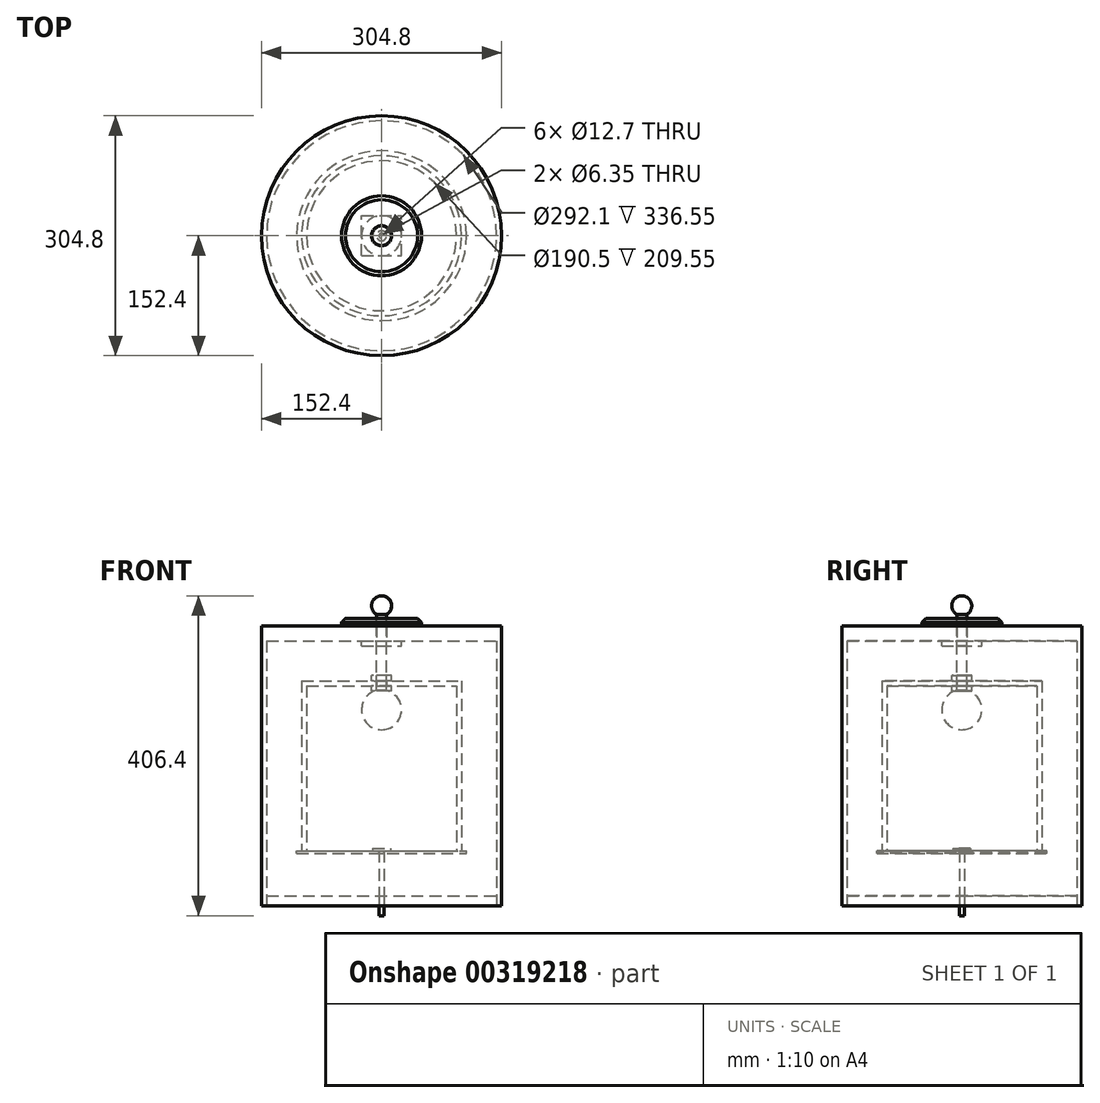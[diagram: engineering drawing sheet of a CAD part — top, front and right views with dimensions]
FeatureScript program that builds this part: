
annotation { "Feature Type Name" : "Feature", "Feature Type Description" : "" }
export const myFeature = defineFeature(function(context is Context, id is Id, definition is map)
    precondition{}
    {
        {
            var Q0;
            Q0=qCreatedBy(makeId("Front.planeOp"),FACE);
            var sketch = newSketch(context, id + "F0", { "sketchPlane" : qUnion([Q0])});
            skLineSegment(sketch, "E0", {"start": v(6.35, 0) * mm, "end": v(152.4, 0) * mm});
            skLineSegment(sketch, "E1", {"start": v(152.4, 0) * mm, "end": v(152.4, -355.6) * mm});
            skLineSegment(sketch, "E2", {"start": v(152.4, -355.6) * mm, "end": v(146.05, -355.6) * mm});
            skLineSegment(sketch, "E3", {"start": v(0, -400.05) * mm, "end": v(0, -355.6) * mm});
            skLineSegment(sketch, "E4", {"start": v(146.05, -349.25) * mm, "end": v(146.05, -19.05) * mm});
            skLineSegment(sketch, "E5", {"start": v(146.05, -19.05) * mm, "end": v(6.35, -19.05) * mm});
            skLineSegment(sketch, "E6", {"start": v(6.35, 0) * mm, "end": v(6.35, -19.05) * mm});
            skPoint(sketch, "E7.orphan", {"position": v(0, -19.05) * mm});
            skLineSegment(sketch, "E8", {"start": v(146.05, -349.25) * mm, "end": v(146.05, -355.6) * mm});
            skSolve(sketch);
        }
        {
            var Q0;
            Q0=makeQuery(id+"F0.imprint","IMPRINT",FACE,{"disambiguationData":[TD([[makeQuery(id+"F0.imprint","IMPRINT",EDGE,{"derivedFrom":sQuery(id+"F0.wireOp",EDGE,"E0")}),-1.0]])]});
            var Q1;
            Q1=sQuery(id+"F0.wireOp",EDGE,"E3");
            revolve(context, id + "F1", {"entities" : qUnion([Q0]), "axis" : qUnion([Q1]), "revolveType" : RevolveType.FULL});
        }
        {
            var Q0;
            Q0=qCreatedBy(makeId("Front.planeOp"),FACE);
            var sketch = newSketch(context, id + "F2", { "sketchPlane" : qUnion([Q0])});
            skLineSegment(sketch, "E9", {"start": v(0, 0) * mm, "end": v(50.8, 0) * mm});
            skLineSegment(sketch, "E10", {"start": v(50.8, 0) * mm, "end": v(50.8, 9.53) * mm});
            skLineSegment(sketch, "E11", {"start": v(50.8, 9.53) * mm, "end": v(6.35, 9.52) * mm});
            skLineSegment(sketch, "E12", {"start": v(0, 12.7) * mm, "end": v(0, 0) * mm});
            skLineSegment(sketch, "E13", {"start": v(6.35, 9.52) * mm, "end": v(6.35, 0) * mm});
            skSolve(sketch);
        }
        {
            var Q0;
            Q0=makeQuery(id+"F2.imprint","IMPRINT",FACE,{"disambiguationData":[TD([[makeQuery(id+"F2.imprint","IMPRINT",EDGE,{"derivedFrom":sQuery(id+"F2.wireOp",EDGE,"E9")}),1.0]])]});
            var Q1;
            Q1=sQuery(id+"F2.wireOp",EDGE,"E12");
            revolve(context, id + "F3", {"entities" : qUnion([Q0]), "axis" : qUnion([Q1]), "revolveType" : RevolveType.FULL});
        }
        {
            var Q0;
            Q0=qCreatedBy(makeId("Front.planeOp"),FACE);
            var sketch = newSketch(context, id + "F4", { "sketchPlane" : qUnion([Q0])});
            skLineSegment(sketch, "E14", {"start": v(0, 0) * mm, "end": v(0, -81.28) * mm});
            skLineSegment(sketch, "E15", {"start": v(6.35, -82.09) * mm, "end": v(6.35, 0) * mm});
            skLineSegment(sketch, "E16", {"start": v(6.35, 0) * mm, "end": v(0, 0) * mm});
            skLineSegment(sketch, "E17", {"start": v(6.35, 0) * mm, "end": v(6.35, 14.4) * mm});
            skArc(sketch, "E18", {"start": v(6.35, 14.4) * mm, "mid": v(12.27, 28.69) * mm, "end": v(0, 38.1) * mm});
            skLineSegment(sketch, "E19", {"start": v(0, 0) * mm, "end": v(0, 38.1) * mm});
            skArc(sketch, "E20", {"start": v(0, -132.08) * mm, "mid": v(25.2, -109.88) * mm, "end": v(6.35, -82.09) * mm});
            skPoint(sketch, "E21.orphan", {"position": v(0, -82.55) * mm});
            skLineSegment(sketch, "E22", {"start": v(0, -81.28) * mm, "end": v(0, -132.08) * mm});
            skSolve(sketch);
        }
        {
            var Q0;
            Q0 = qSketchRegion(id + "F4", true);
            var Q1;
            Q1=sQuery(id+"F4.wireOp",EDGE,"E14");
            revolve(context, id + "F5", {"entities" : qUnion([Q0]), "axis" : qUnion([Q1]), "revolveType" : RevolveType.FULL});
        }
        {
            var Q0;
            Q0=qCreatedBy(makeId("Front.planeOp"),FACE);
            var sketch = newSketch(context, id + "F6", { "sketchPlane" : qUnion([Q0])});
            skLineSegment(sketch, "E23", {"start": v(6.35, -69.85) * mm, "end": v(101.6, -69.85) * mm});
            skLineSegment(sketch, "E24", {"start": v(101.6, -69.85) * mm, "end": v(101.6, -285.75) * mm});
            skLineSegment(sketch, "E25", {"start": v(101.6, -285.75) * mm, "end": v(95.25, -285.75) * mm});
            skLineSegment(sketch, "E26", {"start": v(0, -335.92) * mm, "end": v(0, -285.75) * mm});
            skLineSegment(sketch, "E27", {"start": v(95.25, -330.2) * mm, "end": v(95.25, -76.2) * mm});
            skLineSegment(sketch, "E28", {"start": v(95.25, -76.2) * mm, "end": v(6.35, -76.2) * mm});
            skLineSegment(sketch, "E29", {"start": v(0, -76.2) * mm, "end": v(0, -69.85) * mm});
            skLineSegment(sketch, "E30", {"start": v(95.25, -285.75) * mm, "end": v(95.25, -330.2) * mm});
            skLineSegment(sketch, "E31", {"start": v(6.35, -69.85) * mm, "end": v(6.35, -76.2) * mm});
            skSolve(sketch);
        }
        {
            var Q0;
            Q0 = qSketchRegion(id + "F6", true);
            var Q1;
            Q1=sQuery(id+"F6.wireOp",EDGE,"E29");
            revolve(context, id + "F7", {"entities" : qUnion([Q0]), "axis" : qUnion([Q1]), "revolveType" : RevolveType.FULL});
        }
        {
            var Q0;
            Q0=qCreatedBy(makeId("Front.planeOp"),FACE);
            var sketch = newSketch(context, id + "F8", { "sketchPlane" : qUnion([Q0])});
            skLineSegment(sketch, "E32.bottom", {"start": v(6.35, -69.85) * mm, "end": v(12.7, -69.85) * mm});
            skLineSegment(sketch, "E32.top", {"start": v(6.35, -63.09) * mm, "end": v(12.7, -63.09) * mm});
            skLineSegment(sketch, "E32.left", {"start": v(6.35, -69.85) * mm, "end": v(6.35, -63.09) * mm});
            skLineSegment(sketch, "E32.right", {"start": v(12.7, -69.85) * mm, "end": v(12.7, -63.09) * mm});
            skLineSegment(sketch, "E33.bottom", {"start": v(6.35, -76.2) * mm, "end": v(12.7, -76.2) * mm});
            skLineSegment(sketch, "E33.top", {"start": v(6.35, -82.96) * mm, "end": v(12.7, -82.96) * mm});
            skLineSegment(sketch, "E33.left", {"start": v(6.35, -76.2) * mm, "end": v(6.35, -82.96) * mm});
            skLineSegment(sketch, "E33.right", {"start": v(12.7, -76.2) * mm, "end": v(12.7, -82.96) * mm});
            skLineSegment(sketch, "E34", {"start": v(0, -57.88) * mm, "end": v(0, -89.68) * mm, "construction": true});
            skSolve(sketch);
        }
        {
            var Q0;
            Q0=makeQuery(id+"F8.imprint","IMPRINT",FACE,{"disambiguationData":[TD([[makeQuery(id+"F8.imprint","IMPRINT",EDGE,{"derivedFrom":sQuery(id+"F8.wireOp",EDGE,"E32.bottom")}),1.0]])]});
            var Q1;
            Q1=makeQuery(id+"F8.imprint","IMPRINT",FACE,{"disambiguationData":[TD([[makeQuery(id+"F8.imprint","IMPRINT",EDGE,{"derivedFrom":sQuery(id+"F8.wireOp",EDGE,"E33.bottom")}),-1.0]])]});
            var Q2;
            Q2=sQuery(id+"F8.wireOp",EDGE,"E34");
            revolve(context, id + "F9", {"entities" : qUnion([Q0, Q1]), "axis" : qUnion([Q2]), "revolveType" : RevolveType.FULL});
        }
        {
            var Q0;
            Q0=makeQuery(id+"F7.opRevolve","SWEPT_FACE",FACE,{"disambiguationData":[OSD([sQuery(id+"F6.wireOp",EDGE,"E25")])]});
            var sketch = newSketch(context, id + "F10", { "sketchPlane" : qUnion([Q0])});
            skCircle(sketch, "E35", {"center": v(0, 0) * mm, "radius": 107.95 * mm});
            skCircle(sketch, "E36", {"center": v(0, 0) * mm, "radius": 3.18 * mm});
            skSolve(sketch);
        }
        {
            var Q0;
            Q0=makeQuery(id+"F10.imprint","IMPRINT",FACE,{"disambiguationData":[TD([[makeQuery(id+"F10.imprint","IMPRINT",EDGE,{"derivedFrom":sQuery(id+"F10.wireOp",EDGE,"E35")}),1.0]])]});
            var Q1;
            Q1=makeQuery(id+"F10.imprint","IMPRINT",FACE,{"disambiguationData":[TD([[makeQuery(id+"F10.imprint","IMPRINT",EDGE,{"derivedFrom":makeQuery(id+"F7.opRevolve","SWEPT_EDGE",EDGE,{"disambiguationData":[OSD([sQuery(id+"F6.wireOp",EDGE,"E25"),sQuery(id+"F6.wireOp",EDGE,"E27")])]})}),1.0]])]});
            var Q2;
            {var subQ0=sQuery(id+"F6.wireOp",EDGE,"E25");Q2=makeQuery(id+"F10.imprint","IMPRINT",FACE,{"disambiguationData":[TD([[makeQuery(id+"F10.imprint","IMPRINT",EDGE,{"derivedFrom":makeQuery(id+"F7.opRevolve","SWEPT_EDGE",EDGE,{"disambiguationData":[OSD([sQuery(id+"F6.wireOp",EDGE,"E24"),subQ0])]})}),1.0]])]});}
            extrude(context, id + "F11", {"entities" : qUnion([Q0, Q1, Q2]), "depth" : 3.17 * mm});
        }
        {
            var Q0;
            Q0=makeQuery(id+"F3.opRevolve","SWEPT_EDGE",EDGE,{"disambiguationData":[OSD([sQuery(id+"F2.wireOp",EDGE,"E10"),sQuery(id+"F2.wireOp",EDGE,"E11")])]});
            chamfer(context, id + "F12", {"entities" : qUnion([Q0]), "width" : 5.08 * mm, "tangentPropagation" : true});
        }
        {
            var Q0;
            Q0=qCreatedBy(makeId("Front.planeOp"),FACE);
            var sketch = newSketch(context, id + "F13", { "sketchPlane" : qUnion([Q0])});
            skLineSegment(sketch, "E37", {"start": v(0, -282.58) * mm, "end": v(11.22, -282.58) * mm});
            skLineSegment(sketch, "E38", {"start": v(11.22, -282.58) * mm, "end": v(11.22, -285.75) * mm});
            skLineSegment(sketch, "E39", {"start": v(11.22, -285.75) * mm, "end": v(3.17, -285.75) * mm});
            skLineSegment(sketch, "E40", {"start": v(3.17, -285.75) * mm, "end": v(3.18, -368.3) * mm});
            skLineSegment(sketch, "E41", {"start": v(3.18, -368.3) * mm, "end": v(0, -368.3) * mm});
            skLineSegment(sketch, "E42", {"start": v(0, -368.3) * mm, "end": v(0, -282.58) * mm});
            skSolve(sketch);
        }
        {
            var Q0;
            Q0=makeQuery(id+"F13.imprint","IMPRINT",FACE,{"disambiguationData":[TD([[makeQuery(id+"F13.imprint","IMPRINT",EDGE,{"derivedFrom":sQuery(id+"F13.wireOp",EDGE,"E37")}),-1.0]])]});
            var Q1;
            Q1=sQuery(id+"F13.wireOp",EDGE,"E42");
            revolve(context, id + "F14", {"entities" : qUnion([Q0]), "axis" : qUnion([Q1]), "revolveType" : RevolveType.FULL});
        }
        {
            var Q0;
            Q0=makeQuery(id+"F1.opRevolve","SWEPT_FACE",FACE,{"disambiguationData":[OSD([sQuery(id+"F0.wireOp",EDGE,"E5")])]});
            var sketch = newSketch(context, id + "F15", { "sketchPlane" : qUnion([Q0])});
            skLineSegment(sketch, "E43.bottom", {"start": v(-25.4, 25.4) * mm, "end": v(25.4, 25.4) * mm});
            skLineSegment(sketch, "E43.top", {"start": v(-25.4, -25.4) * mm, "end": v(25.4, -25.4) * mm});
            skLineSegment(sketch, "E43.left", {"start": v(-25.4, 25.4) * mm, "end": v(-25.4, -25.4) * mm});
            skLineSegment(sketch, "E43.right", {"start": v(25.4, 25.4) * mm, "end": v(25.4, -25.4) * mm});
            skPoint(sketch, "E43.middle", {"position": v(0, 0) * mm});
            skSolve(sketch);
        }
        {
            var Q0;
            Q0=makeQuery(id+"F15.imprint","IMPRINT",FACE,{"disambiguationData":[TD([[makeQuery(id+"F15.imprint","IMPRINT",EDGE,{"derivedFrom":sQuery(id+"F15.wireOp",EDGE,"E43.bottom")}),-1.0]])]});
            extrude(context, id + "F16", {"entities" : qUnion([Q0]), "depth" : 6.35 * mm});
        }
        {
            var Q0;
            Q0=makeQuery(id+"F1.opRevolve","SWEPT_FACE",FACE,{"disambiguationData":[OSD([sQuery(id+"F0.wireOp",EDGE,"E2")])]});
            var sketch = newSketch(context, id + "F17", { "sketchPlane" : qUnion([Q0])});
            skCircle(sketch, "E44", {"center": v(0, 0) * mm, "radius": 146.05 * mm});
            skCircle(sketch, "E45", {"center": v(0, 0) * mm, "radius": 3.18 * mm});
            skSolve(sketch);
        }
        {
            var Q0;
            Q0=makeQuery(id+"F17.imprint","IMPRINT",FACE,{"disambiguationData":[TD([[makeQuery(id+"F17.imprint","IMPRINT",EDGE,{"derivedFrom":sQuery(id+"F17.wireOp",EDGE,"E44")}),1.0]])]});
            extrude(context, id + "F18", {"entities" : qUnion([Q0]), "oppositeDirection" : true, "depth" : 12.7 * mm});
        }
    });
